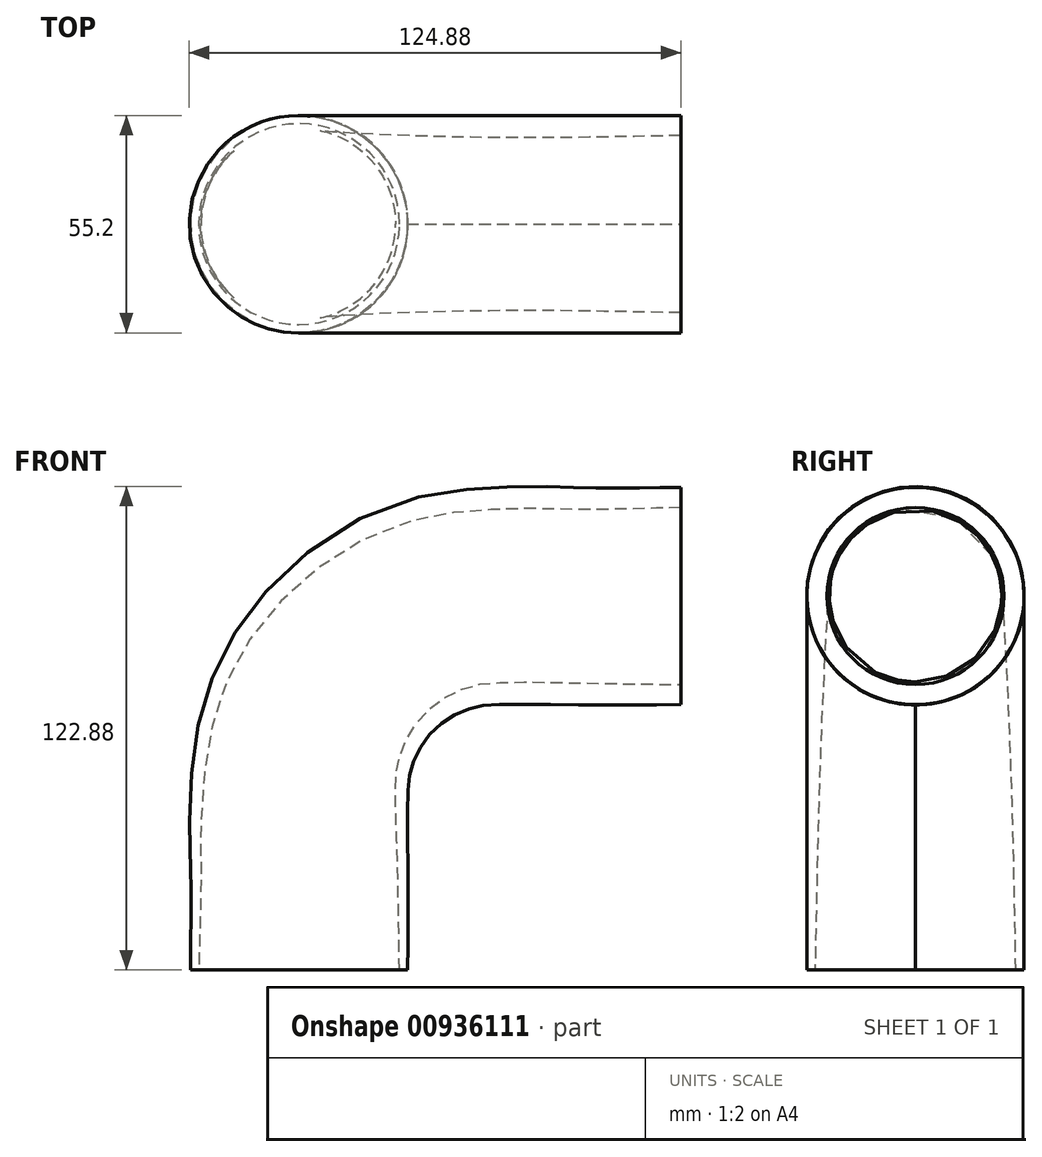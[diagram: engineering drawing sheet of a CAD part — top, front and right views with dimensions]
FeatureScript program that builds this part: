
annotation { "Feature Type Name" : "Feature", "Feature Type Description" : "" }
export const myFeature = defineFeature(function(context is Context, id is Id, definition is map)
    precondition{}
    {
        {
            var Q0;
            Q0=qCreatedBy(makeId("Front.planeOp"),FACE);
            var sketch = newSketch(context, id + "F0", { "sketchPlane" : qUnion([Q0])});
            skLineSegment(sketch, "E0", {"start": v(0, 0) * mm, "end": v(0, 45) * mm});
            skLineSegment(sketch, "E1", {"start": v(50, 95) * mm, "end": v(100, 95) * mm});
            skPoint(sketch, "E2.visualSharp", {"position": v(0, 95) * mm});
            skArc(sketch, "E2.filletArc", {"start": v(50, 95) * mm, "mid": v(14.64, 80.36) * mm, "end": v(0, 45) * mm});
            skSolve(sketch);
        }
        {
            var Q0;
            Q0=qCreatedBy(makeId("Top.planeOp"),FACE);
            var sketch = newSketch(context, id + "F1", { "sketchPlane" : qUnion([Q0])});
            skCircle(sketch, "E3", {"center": v(0, 0) * mm, "radius": 25.5 * mm});
            skSolve(sketch);
        }
        {
            var Q0;
            Q0=qCreatedBy(makeId("Top.planeOp"),FACE);
            cPlane(context, id + "F2", {"entities" : qUnion([Q0]), "cplaneType" : CPlaneType.OFFSET, "offset" : 45 * mm, "width" : 150 * mm, "height" : 150 * mm});
        }
        {
            var Q0;
            Q0=qCreatedBy(id+"F2.planeOp",FACE);
            var sketch = newSketch(context, id + "F3", { "sketchPlane" : qUnion([Q0])});
            skCircle(sketch, "E4", {"center": v(0, 0) * mm, "radius": 24.5 * mm});
            skSolve(sketch);
        }
        {
            var Q0;
            Q0=qCreatedBy(makeId("Right.planeOp"),FACE);
            cPlane(context, id + "F4", {"entities" : qUnion([Q0]), "cplaneType" : CPlaneType.OFFSET, "offset" : 50 * mm, "width" : 150 * mm, "height" : 150 * mm});
        }
        {
            var Q0;
            Q0=qCreatedBy(id+"F4.planeOp",FACE);
            var sketch = newSketch(context, id + "F5", { "sketchPlane" : qUnion([Q0])});
            skPoint(sketch, "E5.0", {"position": v(0, 95) * mm});
            skCircle(sketch, "E6", {"center": v(0, 95) * mm, "radius": 22 * mm});
            skSolve(sketch);
        }
        {
            var Q0;
            Q0=qCreatedBy(id+"F4.planeOp",FACE);
            cPlane(context, id + "F6", {"entities" : qUnion([Q0]), "cplaneType" : CPlaneType.OFFSET, "offset" : 47 * mm, "width" : 150 * mm, "height" : 150 * mm});
        }
        {
            var Q0;
            Q0=qCreatedBy(id+"F6.planeOp",FACE);
            var sketch = newSketch(context, id + "F7", { "sketchPlane" : qUnion([Q0])});
            skPoint(sketch, "E7.0", {"position": v(0, 95) * mm});
            skCircle(sketch, "E8", {"center": v(0, 95) * mm, "radius": 22.5 * mm});
            skSolve(sketch);
        }
        {
            var Q0;
            Q0=sQuery(id+"F0.wireOp",EDGE,"E2.filletArc");
            var Q1;
            Q1=sQuery(id+"F0.wireOp",EDGE,"E0");
            var Q2;
            Q2=sQuery(id+"F0.wireOp",EDGE,"E1");
            var Q3;
            Q3=makeQuery(id+"F1.imprint","IMPRINT",FACE,{"disambiguationData":[TD([[makeQuery(id+"F1.imprint","IMPRINT",EDGE,{"derivedFrom":sQuery(id+"F1.wireOp",EDGE,"E3")}),1.0]])]});
            var Q4;
            Q4=makeQuery(id+"F3.imprint","IMPRINT",FACE,{"disambiguationData":[TD([[makeQuery(id+"F3.imprint","IMPRINT",EDGE,{"derivedFrom":sQuery(id+"F3.wireOp",EDGE,"E4")}),1.0]])]});
            var Q5;
            Q5=makeQuery(id+"F5.imprint","IMPRINT",FACE,{"disambiguationData":[TD([[makeQuery(id+"F5.imprint","IMPRINT",EDGE,{"derivedFrom":sQuery(id+"F5.wireOp",EDGE,"E6")}),1.0]])]});
            var Q6;
            Q6=makeQuery(id+"F7.imprint","IMPRINT",FACE,{"disambiguationData":[TD([[makeQuery(id+"F7.imprint","IMPRINT",EDGE,{"derivedFrom":sQuery(id+"F7.wireOp",EDGE,"E8")}),1.0]])]});
            loft(context, id + "F8", {"addSections" : true, "spine" : qUnion([Q0, Q1, Q2]), "sectionCount" : 5, "sheetProfilesArray" : [{ "sheetProfileEntities" : qUnion([Q3]) }, { "sheetProfileEntities" : qUnion([Q4]) }, { "sheetProfileEntities" : qUnion([Q5]) }, { "sheetProfileEntities" : qUnion([Q6]) }]});
        }
        {
            var Q0;
            Q0=qCreatedBy(makeId("Top.planeOp"),FACE);
            var sketch = newSketch(context, id + "F9", { "sketchPlane" : qUnion([Q0])});
            skCircle(sketch, "E9", {"center": v(0, 0) * mm, "radius": 27.6 * mm});
            skSolve(sketch);
        }
        {
            var Q0;
            Q0=qCreatedBy(id+"F2.planeOp",FACE);
            var sketch = newSketch(context, id + "F10", { "sketchPlane" : qUnion([Q0])});
            skCircle(sketch, "E10.0", {"center": v(0, 0) * mm, "radius": 27.6 * mm});
            skSolve(sketch);
        }
        {
            var Q0;
            Q0=qCreatedBy(id+"F4.planeOp",FACE);
            var sketch = newSketch(context, id + "F11", { "sketchPlane" : qUnion([Q0])});
            skPoint(sketch, "E11.0", {"position": v(0, 95) * mm});
            skCircle(sketch, "E12", {"center": v(0, 95) * mm, "radius": 27.6 * mm});
            skSolve(sketch);
        }
        {
            var Q0;
            Q0=qCreatedBy(id+"F6.planeOp",FACE);
            var sketch = newSketch(context, id + "F12", { "sketchPlane" : qUnion([Q0])});
            skCircle(sketch, "E13.0", {"center": v(0, 95) * mm, "radius": 27.6 * mm});
            skSolve(sketch);
        }
        {
            var Q0;
            Q0 = qConstructionFilter(qBodyType(qCreatedBy(id + "F0" ,EDGE), BodyType.WIRE), ConstructionObject.NO);
            var Q1;
            Q1 = qSketchRegion(id + "F9", true);
            var Q2;
            Q2 = qSketchRegion(id + "F10", true);
            var Q3;
            Q3 = qSketchRegion(id + "F11", true);
            var Q4;
            Q4 = qSketchRegion(id + "F12", true);
            loft(context, id + "F13", {"addSections" : true, "spine" : qUnion([Q0]), "sectionCount" : 5, "sheetProfilesArray" : [{ "sheetProfileEntities" : qUnion([Q1]) }, { "sheetProfileEntities" : qUnion([Q2]) }, { "sheetProfileEntities" : qUnion([Q3]) }, { "sheetProfileEntities" : qUnion([Q4]) }]});
        }
        {
            var Q0;
            Q0=makeQuery(id+"F8.opLoft","SWEPT_BODY",BODY,{"disambiguationData":[OSD([makeQuery(id+"F1.imprint","IMPRINT",FACE,{"disambiguationData":[TD([[makeQuery(id+"F1.imprint","IMPRINT",EDGE,{"derivedFrom":sQuery(id+"F1.wireOp",EDGE,"E3")}),1.0]])]}),sQuery(id+"F3.wireOp",EDGE,"E4"),sQuery(id+"F5.wireOp",EDGE,"E6"),makeQuery(id+"F7.imprint","IMPRINT",FACE,{"disambiguationData":[TD([[makeQuery(id+"F7.imprint","IMPRINT",EDGE,{"derivedFrom":sQuery(id+"F7.wireOp",EDGE,"E8")}),1.0]])]})])]});
            var Q1;
            Q1=makeQuery(id+"F13.opLoft","SWEPT_BODY",BODY,{"disambiguationData":[OSD([makeQuery(id+"F9.imprint","IMPRINT",FACE,{"disambiguationData":[TD([[makeQuery(id+"F9.imprint","IMPRINT",EDGE,{"derivedFrom":sQuery(id+"F9.wireOp",EDGE,"E9")}),1.0]])]}),sQuery(id+"F10.wireOp",EDGE,"E10.0"),sQuery(id+"F11.wireOp",EDGE,"E12"),makeQuery(id+"F12.imprint","IMPRINT",FACE,{"disambiguationData":[TD([[makeQuery(id+"F12.imprint","IMPRINT",EDGE,{"derivedFrom":sQuery(id+"F12.wireOp",EDGE,"E13.0")}),1.0]])]})])]});
            booleanBodies(context, id + "F14", {"operationType" : BooleanOperationType.SUBTRACTION, "tools" : qUnion([Q0]), "targets" : qUnion([Q1])});
        }
    });
